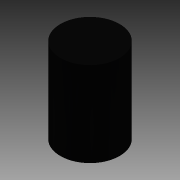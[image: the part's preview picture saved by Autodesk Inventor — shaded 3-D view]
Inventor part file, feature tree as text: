
AUTODESK INVENTOR PART (.ipt)
format: ipt  version: 2015 (Build 190159000, 159)  size: 69,120 bytes
history: native  units: in
note: dims shown in document units (in); Inventor stores cm internally (conversion verified against a paired STEP export)
features: extrude x1, sketch x1
ambient origin geometry x8: Origin, YZ Plane, XZ Plane, XY Plane, X Axis, Y Axis, Z Axis, Center Point
bodies: Solid1 (feature_tree)
feature tree (2):
  extrude  "Extrusion1"  Depth=2.15in TaperAngle=0.0deg
  sketch  "Sketch1"  dims[d0=1.5in d1=2.15in d2=0.0in]
